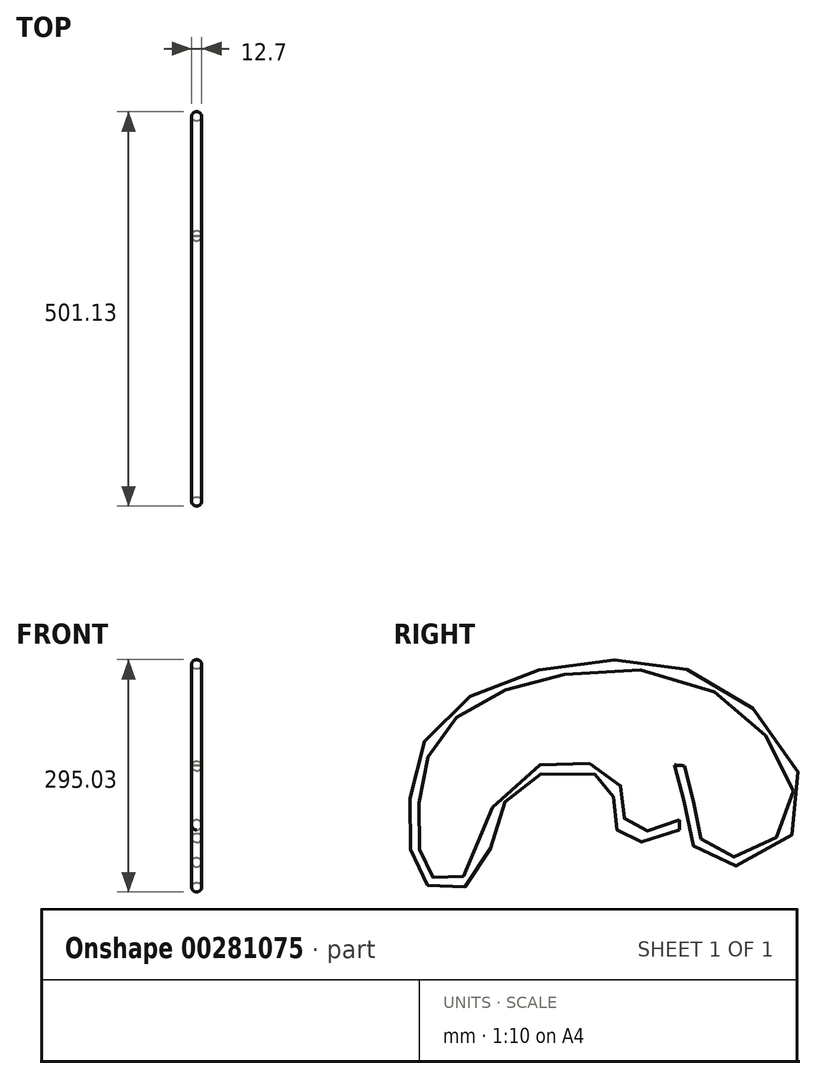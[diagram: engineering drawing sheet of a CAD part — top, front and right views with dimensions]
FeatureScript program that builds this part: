
annotation { "Feature Type Name" : "Feature", "Feature Type Description" : "" }
export const myFeature = defineFeature(function(context is Context, id is Id, definition is map)
    precondition{}
    {
        {
            var Q0;
            Q0=qCreatedBy(makeId("Right.planeOp"),FACE);
            var sketch = newSketch(context, id + "F0", { "sketchPlane" : qUnion([Q0])});
            skFitSpline(sketch, "E0", {"points": [v(0, 0) * mm, v(-54.41, -16.18) * mm, v(-70.77, -10.5) * mm, v(-77.53, 23.65) * mm, v(-93.41, 64.08) * mm, v(-206.04, 58.3) * mm, v(-244.3, -24) * mm, v(-284, -77.42) * mm, v(-323.72, -65.15) * mm, v(-337.43, 0) * mm, v(-307.83, 120.4) * mm, v(-136, 199.09) * mm, v(63.98, 163.71) * mm, v(147, 6.32) * mm, v(41.6, -44.21) * mm, v(13.44, 19.32) * mm, v(0, 75.63) * mm], "startDerivative": vector(-1190.08, -441.83) * mm, "endDerivative": vector(-283.24, 987) * mm});
            skSolve(sketch);
        }
        {
            var Q0;
            Q0=qCreatedBy(makeId("Front.planeOp"),FACE);
            var sketch = newSketch(context, id + "F1", { "sketchPlane" : qUnion([Q0])});
            skCircle(sketch, "E1", {"center": v(0, 0) * mm, "radius": 6.35 * mm});
            skSolve(sketch);
        }
        {
            var Q0;
            Q0=makeQuery(id+"F1.imprint","IMPRINT",FACE,{"disambiguationData":[TD([[makeQuery(id+"F1.imprint","IMPRINT",EDGE,{"derivedFrom":sQuery(id+"F1.wireOp",EDGE,"E1")}),1.0]])]});
            var Q1;
            Q1=sQuery(id+"F0.wireOp",EDGE,"E0");
            sweep(context, id + "F2", {"profiles" : qUnion([Q0]), "path" : qUnion([Q1])});
        }
    });
